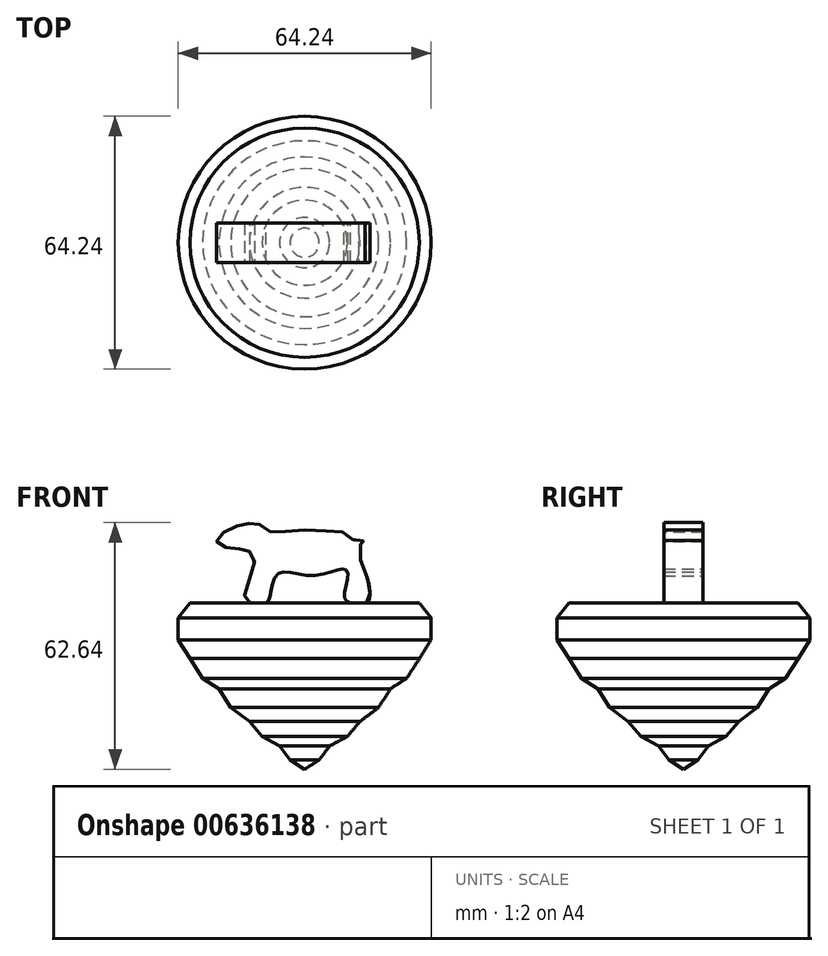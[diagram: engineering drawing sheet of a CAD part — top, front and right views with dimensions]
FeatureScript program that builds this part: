
annotation { "Feature Type Name" : "Feature", "Feature Type Description" : "" }
export const myFeature = defineFeature(function(context is Context, id is Id, definition is map)
    precondition{}
    {
        {
            var Q0;
            Q0=qCreatedBy(makeId("Front.planeOp"),FACE);
            var sketch = newSketch(context, id + "F0", { "sketchPlane" : qUnion([Q0])});
            skLineSegment(sketch, "E0", {"start": v(0, 0) * mm, "end": v(0, -42.19) * mm});
            skLineSegment(sketch, "E1", {"start": v(0, -42.19) * mm, "end": v(-3.7, -39.82) * mm});
            skLineSegment(sketch, "E2", {"start": v(-3.7, -39.82) * mm, "end": v(-6.37, -36.27) * mm});
            skLineSegment(sketch, "E3", {"start": v(-6.37, -36.27) * mm, "end": v(-10.8, -33.9) * mm});
            skLineSegment(sketch, "E4", {"start": v(-10.8, -33.9) * mm, "end": v(-14.06, -30.05) * mm});
            skLineSegment(sketch, "E5", {"start": v(-14.06, -30.05) * mm, "end": v(-18.8, -26.5) * mm});
            skLineSegment(sketch, "E6", {"start": v(-18.8, -26.5) * mm, "end": v(-21.76, -21.76) * mm});
            skLineSegment(sketch, "E7", {"start": v(-21.76, -21.76) * mm, "end": v(-25.9, -19.1) * mm});
            skLineSegment(sketch, "E8", {"start": v(-25.9, -19.1) * mm, "end": v(-29.16, -14.06) * mm});
            skLineSegment(sketch, "E9", {"start": v(-29.16, -14.06) * mm, "end": v(-32.12, -9.33) * mm});
            skLineSegment(sketch, "E10", {"start": v(-32.12, -9.33) * mm, "end": v(-32.12, -3.7) * mm});
            skLineSegment(sketch, "E11", {"start": v(-32.12, -3.7) * mm, "end": v(-29.11, 0) * mm});
            skLineSegment(sketch, "E12", {"start": v(-29.11, 0) * mm, "end": v(0, 0) * mm});
            skSolve(sketch);
        }
        {
            var Q0;
            Q0 = qSketchRegion(id + "F0", true);
            var Q1;
            Q1=sQuery(id+"F0.wireOp",EDGE,"E0");
            revolve(context, id + "F1", {"entities" : qUnion([Q0]), "axis" : qUnion([Q1]), "revolveType" : RevolveType.FULL});
        }
        {
            var Q0;
            Q0=qCreatedBy(makeId("Front.planeOp"),FACE);
            var sketch = newSketch(context, id + "F2", { "sketchPlane" : qUnion([Q0])});
            skFitSpline(sketch, "E13", {"points": [v(-13.89, 0) * mm, v(-15.3, 1.48) * mm, v(-13.36, 7.81) * mm, v(-13.18, 12.4) * mm, v(-15.47, 13.62) * mm, v(-18.11, 13.8) * mm, v(-22.16, 15.2) * mm, v(-21.98, 16.61) * mm, v(-18.29, 19.26) * mm, v(-14.6, 20.14) * mm, v(-11.95, 20.31) * mm, v(-8.78, 18.2) * mm, v(-3.68, 18.38) * mm, v(5.83, 18.38) * mm, v(10.93, 17.5) * mm, v(13.22, 15.56) * mm, v(15.33, 15.91) * mm, v(13.93, 14.5) * mm, v(15.51, 7.46) * mm, v(16.57, 2.36) * mm, v(15.69, 0) * mm, v(11.64, 0) * mm, v(10.05, 1.83) * mm, v(10.93, 7.64) * mm, v(9.53, 8.7) * mm, v(1.78, 6.93) * mm, v(-6.5, 7.64) * mm, v(-8.6, 2.7) * mm, v(-9.84, 0) * mm, v(-13.89, 0) * mm]});
            skSolve(sketch);
        }
        {
            var Q0;
            Q0 = qSketchRegion(id + "F2", true);
            extrude(context, id + "F3", {"entities" : qUnion([Q0]), "operationType" : NewBodyOperationType.ADD, "endBound" : BoundingType.SYMMETRIC, "depth" : 10 * mm, "offsetDistance" : 25 * mm});
        }
    });
